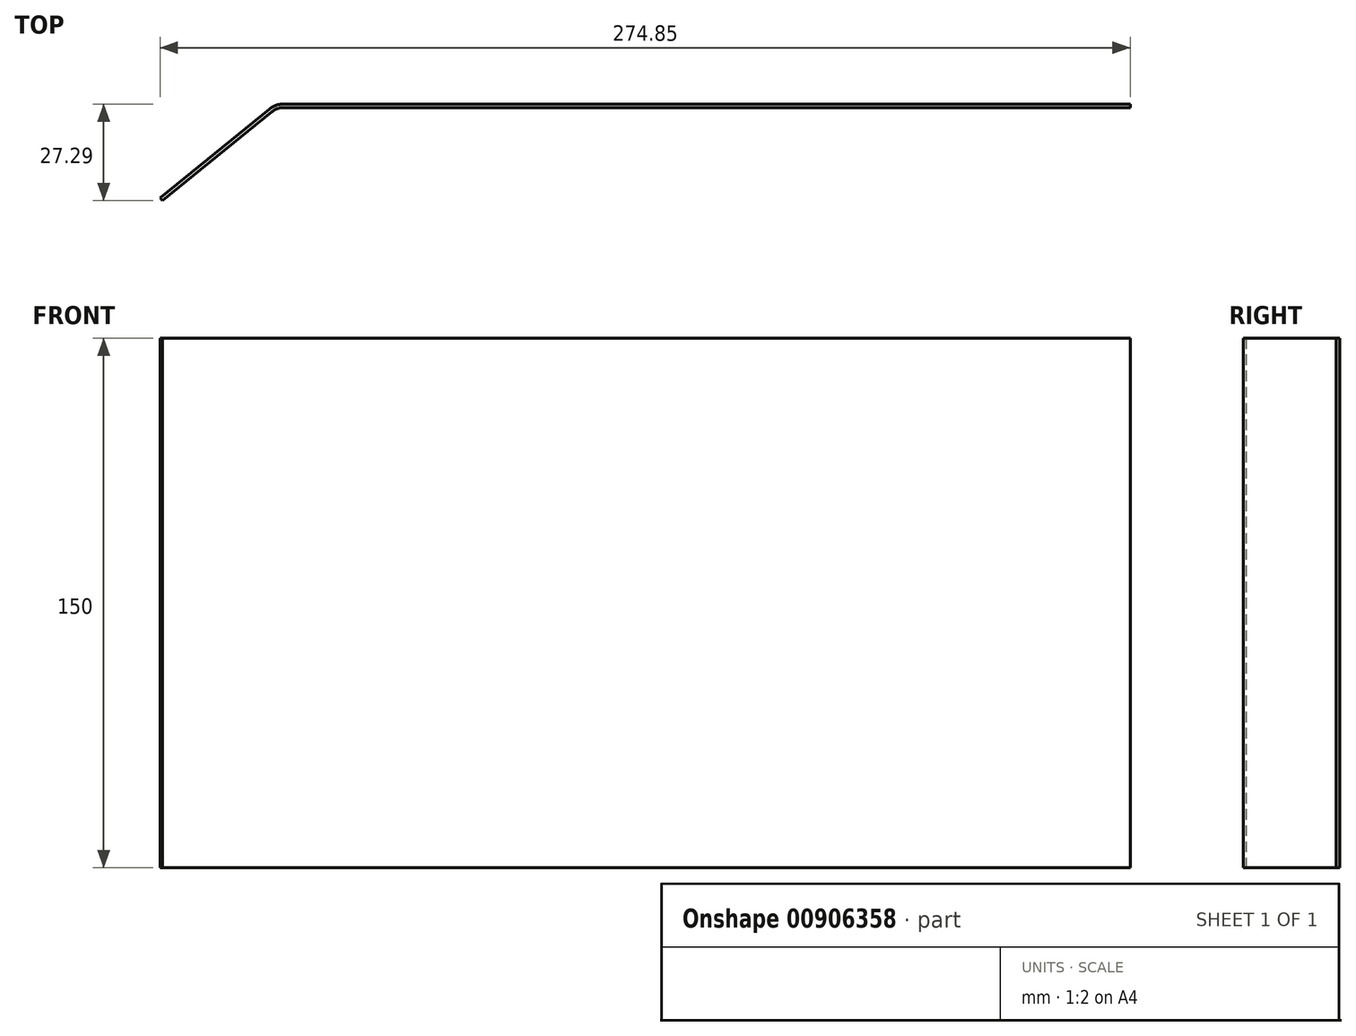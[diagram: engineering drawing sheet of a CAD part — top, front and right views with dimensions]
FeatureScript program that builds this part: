
annotation { "Feature Type Name" : "Feature", "Feature Type Description" : "" }
export const myFeature = defineFeature(function(context is Context, id is Id, definition is map)
    precondition{}
    {
        {
            var Q0;
            Q0=qCreatedBy(makeId("Front.planeOp"),FACE);
            var sketch = newSketch(context, id + "F0", { "sketchPlane" : qUnion([Q0])});
            skLineSegment(sketch, "E0.bottom", {"start": v(-81.4, 76.14) * mm, "end": v(158.6, 76.14) * mm});
            skLineSegment(sketch, "E0.top", {"start": v(-81.4, -73.86) * mm, "end": v(158.6, -73.86) * mm});
            skLineSegment(sketch, "E0.left", {"start": v(-81.4, 76.14) * mm, "end": v(-81.4, -73.86) * mm});
            skLineSegment(sketch, "E0.right", {"start": v(158.6, 76.14) * mm, "end": v(158.6, -73.86) * mm});
            skSolve(sketch);
        }
        {
            var Q0;
            Q0=makeQuery(id+"F0.imprint","IMPRINT",FACE,{"disambiguationData":[TD([[makeQuery(id+"F0.imprint","IMPRINT",EDGE,{"derivedFrom":sQuery(id+"F0.wireOp",EDGE,"E0.bottom")}),-1.0]])]});
            extrude(context, id + "F1", {"entities" : qUnion([Q0]), "depth" : 1 * mm, "offsetDistance" : 25 * mm});
        }
        {
            var Q0;
            Q0=makeQuery(id+"F1.opExtrude","CAP_FACE",FACE,{"disambiguationData":[OSD([sQuery(id+"F0.wireOp",EDGE,"E0.bottom"),sQuery(id+"F0.wireOp",EDGE,"E0.top"),sQuery(id+"F0.wireOp",EDGE,"E0.left"),sQuery(id+"F0.wireOp",EDGE,"E0.right")])],"isStart":false});
            var sketch = newSketch(context, id + "F2", { "sketchPlane" : qUnion([Q0])});
            skPoint(sketch, "E1", {"position": v(-81.4, -71.86) * mm});
            skLineSegment(sketch, "E2", {"start": v(-81.4, -71.86) * mm, "end": v(158.6, -71.86) * mm, "construction": true});
            skSolve(sketch);
        }
        {
            var Q0;
            Q0=makeQuery(id+"F1.opExtrude","SWEPT_FACE",FACE,{"disambiguationData":[OSD([sQuery(id+"F0.wireOp",EDGE,"E0.top")])]});
            var sketch = newSketch(context, id + "F3", { "sketchPlane" : qUnion([Q0])});
            skLineSegment(sketch, "E3", {"start": v(-84.54, 2.11) * mm, "end": v(-115.62, 27.29) * mm});
            skLineSegment(sketch, "E4", {"start": v(-81.4, 1) * mm, "end": v(-73.26, 1) * mm});
            skPoint(sketch, "E5.visualSharp", {"position": v(-81.4, 1) * mm});
            skArc(sketch, "E5.filletArc", {"start": v(-84.54, 2.11) * mm, "mid": v(-83.06, 1.29) * mm, "end": v(-81.4, 1) * mm});
            skSolve(sketch);
        }
        {
            var Q0;
            Q0=makeQuery(id+"F1.opExtrude","SWEPT_FACE",FACE,{"disambiguationData":[OSD([sQuery(id+"F0.wireOp",EDGE,"E0.left")])]});
            var sketch = newSketch(context, id + "F4", { "sketchPlane" : qUnion([Q0])});
            skLineSegment(sketch, "E6.0.0", {"start": v(0, 76.14) * mm, "end": v(0, -73.86) * mm});
            skLineSegment(sketch, "E6.0.1", {"start": v(0, -73.86) * mm, "end": v(1, -73.86) * mm});
            skLineSegment(sketch, "E6.0.2", {"start": v(1, -73.86) * mm, "end": v(1, 76.14) * mm});
            skLineSegment(sketch, "E6.0.3", {"start": v(1, 76.14) * mm, "end": v(0, 76.14) * mm});
            skSolve(sketch);
        }
        {
            var Q0;
            Q0=makeQuery(id+"F4.imprint","IMPRINT",FACE,{"disambiguationData":[TD([[makeQuery(id+"F4.imprint","IMPRINT",EDGE,{"derivedFrom":sQuery(id+"F4.wireOp",EDGE,"E6.0.0")}),1.0]])]});
            var Q1;
            Q1=sQuery(id+"F3.wireOp",EDGE,"E3");
            var Q2;
            Q2=sQuery(id+"F3.wireOp",EDGE,"E5.filletArc");
            sweep(context, id + "F5", {"operationType" : NewBodyOperationType.ADD, "profiles" : qUnion([Q0]), "path" : qUnion([Q1, Q2])});
        }
    });
